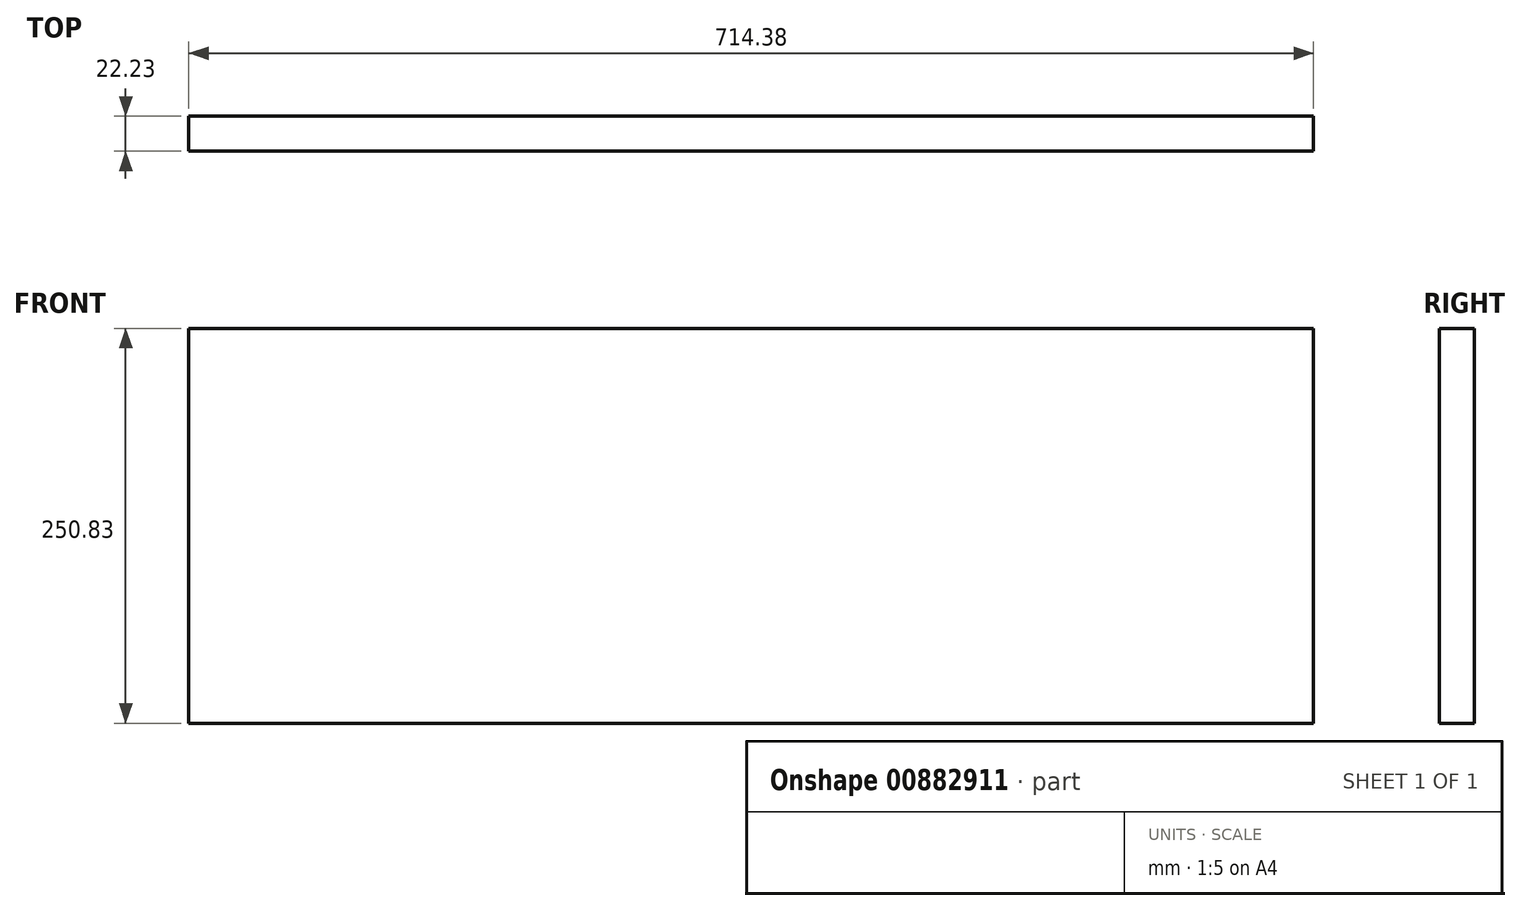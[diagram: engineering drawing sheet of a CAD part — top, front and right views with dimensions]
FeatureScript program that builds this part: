
annotation { "Feature Type Name" : "Feature", "Feature Type Description" : "" }
export const myFeature = defineFeature(function(context is Context, id is Id, definition is map)
    precondition{}
    {
        {
            var Q0;
            Q0=qCreatedBy(makeId("Front.planeOp"),FACE);
            var sketch = newSketch(context, id + "F0", { "sketchPlane" : qUnion([Q0])});
            skLineSegment(sketch, "E0.bottom", {"start": v(0, 0) * mm, "end": v(714.38, 0) * mm});
            skLineSegment(sketch, "E0.top", {"start": v(0, -250.83) * mm, "end": v(714.38, -250.83) * mm});
            skLineSegment(sketch, "E0.left", {"start": v(0, 0) * mm, "end": v(0, -250.83) * mm});
            skLineSegment(sketch, "E0.right", {"start": v(714.38, 0) * mm, "end": v(714.38, -250.82) * mm});
            skSolve(sketch);
        }
        {
            var Q0;
            Q0=makeQuery(id+"F0.imprint","IMPRINT",FACE,{"disambiguationData":[TD([[makeQuery(id+"F0.imprint","IMPRINT",EDGE,{"derivedFrom":sQuery(id+"F0.wireOp",EDGE,"E0.bottom")}),-1.0]])]});
            extrude(context, id + "F1", {"entities" : qUnion([Q0]), "depth" : 22.22 * mm, "offsetDistance" : 25.4 * mm});
        }
    });
